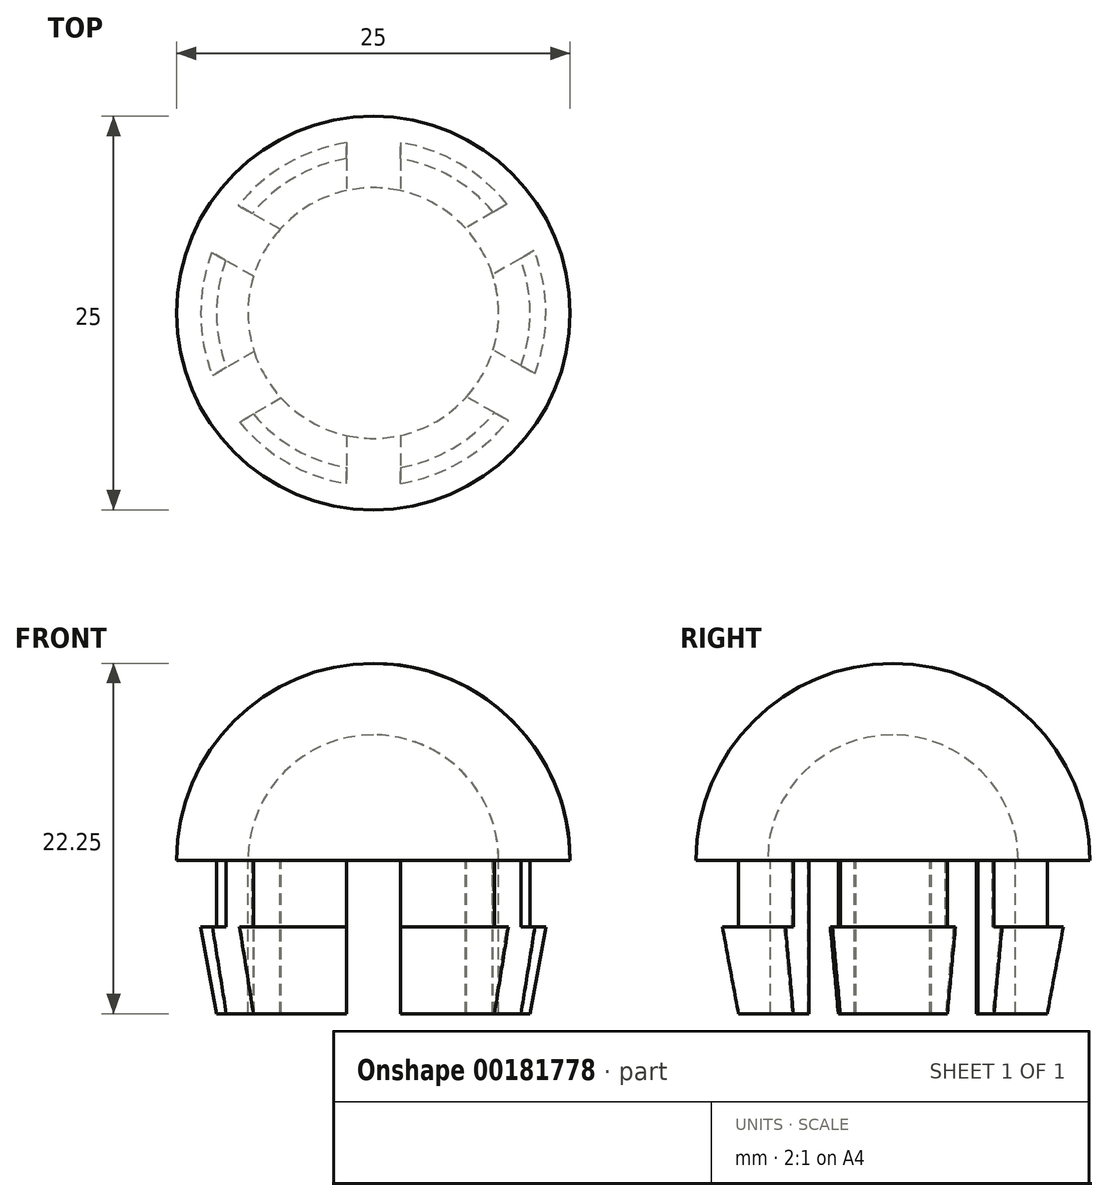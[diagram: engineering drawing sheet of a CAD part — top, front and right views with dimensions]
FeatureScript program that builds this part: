
annotation { "Feature Type Name" : "Feature", "Feature Type Description" : "" }
export const myFeature = defineFeature(function(context is Context, id is Id, definition is map)
    precondition{}
    {
        {
            var Q0;
            Q0=qCreatedBy(makeId("Front.planeOp"),FACE);
            var sketch = newSketch(context, id + "F0", { "sketchPlane" : qUnion([Q0])});
            skArc(sketch, "E0", {"start": v(-12.5, 0) * mm, "mid": v(-8.84, 8.84) * mm, "end": v(0, 12.5) * mm});
            skLineSegment(sketch, "E1", {"start": v(-12.5, 0) * mm, "end": v(-9.96, 0) * mm});
            skLineSegment(sketch, "E2", {"start": v(-9.96, 0) * mm, "end": v(-9.96, -4.25) * mm});
            skLineSegment(sketch, "E3", {"start": v(-9.96, -4.25) * mm, "end": v(-9.96, -4.25) * mm});
            skLineSegment(sketch, "E4", {"start": v(-9.96, -4.25) * mm, "end": v(-10.96, -4.25) * mm});
            skLineSegment(sketch, "E5", {"start": v(-10.96, -4.25) * mm, "end": v(-9.96, -9.75) * mm});
            skLineSegment(sketch, "E6", {"start": v(-9.96, -9.75) * mm, "end": v(-7.96, -9.75) * mm});
            skLineSegment(sketch, "E7", {"start": v(-7.96, -9.75) * mm, "end": v(-7.96, 0) * mm});
            skArc(sketch, "E8", {"start": v(-7.96, 0) * mm, "mid": v(-5.63, 5.63) * mm, "end": v(0, 7.96) * mm});
            skLineSegment(sketch, "E9", {"start": v(0, 12.5) * mm, "end": v(0, 7.96) * mm});
            skSolve(sketch);
        }
        {
            var Q0;
            Q0 = qSketchRegion(id + "F0", true);
            var Q1;
            Q1=sQuery(id+"F0.wireOp",EDGE,"E9");
            revolve(context, id + "F3", {"entities" : qUnion([Q0]), "axis" : qUnion([Q1]), "revolveType" : RevolveType.FULL});
        }
        {
            var Q0;
            Q0=qCreatedBy(makeId("Top.planeOp"),FACE);
            var sketch = newSketch(context, id + "F1", { "sketchPlane" : qUnion([Q0])});
            skLineSegment(sketch, "E10.bottom", {"start": v(1.71, 21.6) * mm, "end": v(-1.71, 21.6) * mm});
            skLineSegment(sketch, "E10.top", {"start": v(1.71, -21.6) * mm, "end": v(-1.71, -21.6) * mm});
            skLineSegment(sketch, "E10.left", {"start": v(1.71, 21.6) * mm, "end": v(1.71, -21.6) * mm});
            skLineSegment(sketch, "E10.right", {"start": v(-1.71, 21.6) * mm, "end": v(-1.71, -21.6) * mm});
            skPoint(sketch, "E10.middle", {"position": v(0, 0) * mm});
            skLineSegment(sketch, "E11.1.0", {"start": v(19.52, 9.4) * mm, "end": v(-17.8, -12.36) * mm});
            skLineSegment(sketch, "E11.1.1", {"start": v(19.52, 9.4) * mm, "end": v(17.8, 12.36) * mm});
            skLineSegment(sketch, "E11.1.2", {"start": v(17.8, 12.36) * mm, "end": v(-19.52, -9.4) * mm});
            skLineSegment(sketch, "E11.1.3", {"start": v(-17.8, -12.36) * mm, "end": v(-19.52, -9.4) * mm});
            skLineSegment(sketch, "E11.2.0", {"start": v(17.95, -12.13) * mm, "end": v(-19.64, 9.15) * mm});
            skLineSegment(sketch, "E11.2.1", {"start": v(17.95, -12.13) * mm, "end": v(19.64, -9.15) * mm});
            skLineSegment(sketch, "E11.2.2", {"start": v(19.64, -9.15) * mm, "end": v(-17.95, 12.13) * mm});
            skLineSegment(sketch, "E11.2.3", {"start": v(-19.64, 9.15) * mm, "end": v(-17.95, 12.13) * mm});
            skLineSegment(sketch, "E11.anchor1", {"start": v(0, 0) * mm, "end": v(1.71, -21.6) * mm, "construction": true});
            skLineSegment(sketch, "E11.anchor2", {"start": v(0, 0) * mm, "end": v(-19.64, 9.15) * mm, "construction": true});
            skSolve(sketch);
        }
        {
            var Q0;
            Q0 = qSketchRegion(id + "F1", true);
            var Q1;
            Q1=makeQuery(id+"F3.opRevolve","SWEPT_FACE",FACE,{"disambiguationData":[OSD([sQuery(id+"F0.wireOp",EDGE,"E6")])]});
            extrude(context, id + "F2", {"entities" : qUnion([Q0, Q1]), "operationType" : NewBodyOperationType.REMOVE, "endBound" : BoundingType.THROUGH_ALL, "oppositeDirection" : true, "depth" : 25.4 * mm});
        }
    });
